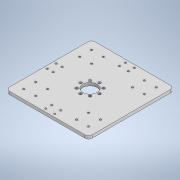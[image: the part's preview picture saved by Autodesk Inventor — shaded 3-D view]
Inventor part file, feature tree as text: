
AUTODESK INVENTOR PART (.ipt)
format: ipt  version: 2021 (Build 250183000, 183)  size: 281,600 bytes
history: native  units: mm
features: other x9, sketch x7, hole x4, mirror x3, pattern_circular x1
ambient origin geometry x8: Origin, YZ Plane, XZ Plane, XY Plane, X Axis, Y Axis, Z Axis, Center Point
bodies: Body1 (feature_tree)
feature tree (24):
  other  "實體1"
  hole  "孔1"  [1 undecoded]
  pattern_circular  "環形陣列1"  [2 undecoded]
  hole  "孔2"  [1 undecoded]
  hole  "孔3"  [1 undecoded]
  mirror  "鏡射1"
  other  "凸緣1"
  hole  "孔4"  [1 undecoded]
  mirror  "鏡射2"
  mirror  "鏡射3"
  other  "轉角外圓角2"
  sketch  "草圖1"
  other  "平板1"
  sketch  "草圖2"
  sketch  "草圖3"
  sketch  "草圖4"
  sketch  "草圖5"
  sketch  "草圖6"
  other  "平板2"
  other  "折彎1"
  other  "轉角1"
  sketch  "草圖7"
  other  "切割1"
  other  "定義1"
note: 6 required parameter values undecoded (feature->parameter linkage not recoverable at this tier; creation-order binding heuristic only, values carry confidence <= 0.55)
